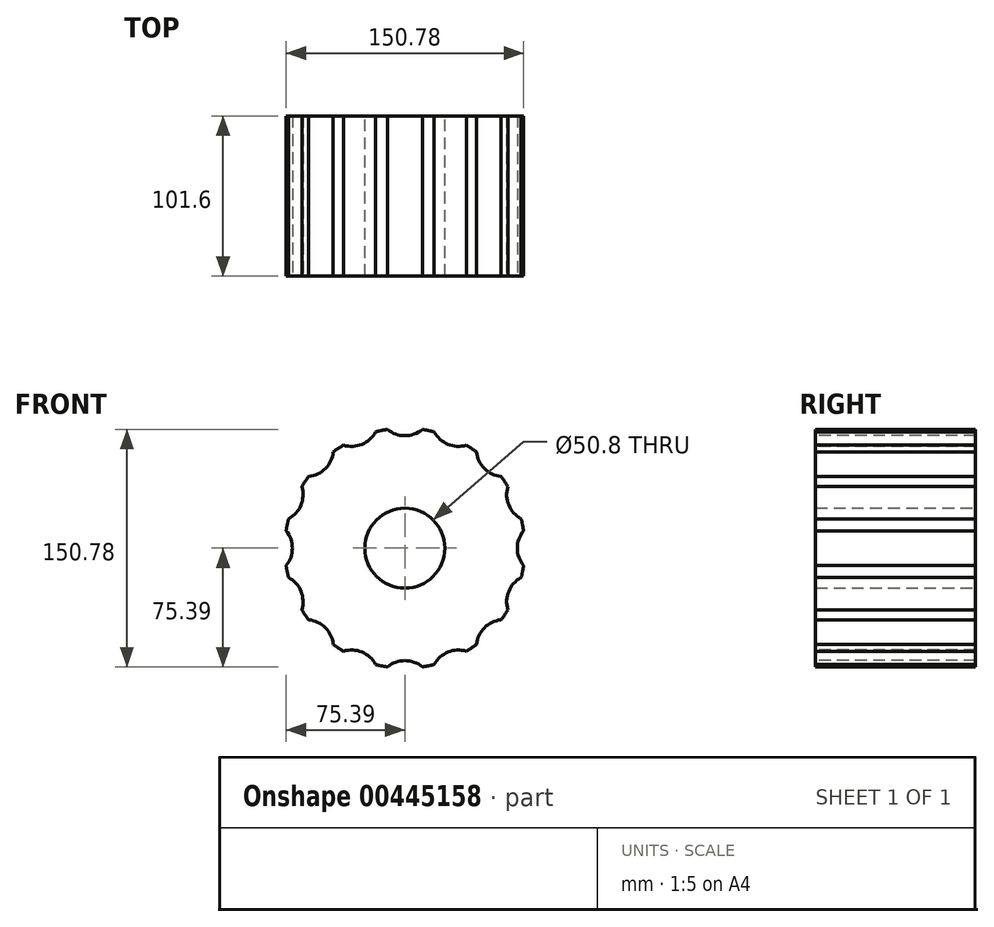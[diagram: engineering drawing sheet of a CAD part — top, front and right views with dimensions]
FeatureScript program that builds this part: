
annotation { "Feature Type Name" : "Feature", "Feature Type Description" : "" }
export const myFeature = defineFeature(function(context is Context, id is Id, definition is map)
    precondition{}
    {
        {
            var Q0;
            Q0=qCreatedBy(makeId("Front.planeOp"),FACE);
            var sketch = newSketch(context, id + "F0", { "sketchPlane" : qUnion([Q0])});
            skCircle(sketch, "E0", {"center": v(0, 0) * mm, "radius": 25.4 * mm});
            skCircle(sketch, "E1", {"center": v(0, 0) * mm, "radius": 76.2 * mm});
            skSolve(sketch);
        }
        {
            var Q0;
            Q0=makeQuery(id+"F0.imprint","IMPRINT",FACE,{"disambiguationData":[TD([[makeQuery(id+"F0.imprint","IMPRINT",EDGE,{"derivedFrom":sQuery(id+"F0.wireOp",EDGE,"E0")}),-1.0]])]});
            extrude(context, id + "F1", {"entities" : qUnion([Q0]), "depth" : 101.6 * mm});
        }
        {
            var Q0;
            Q0=makeQuery(id+"F1.opExtrude","CAP_FACE",FACE,{"disambiguationData":[OSD([sQuery(id+"F0.wireOp",EDGE,"E0"),sQuery(id+"F0.wireOp",EDGE,"E1")])],"isStart":false});
            var sketch = newSketch(context, id + "F2", { "sketchPlane" : qUnion([Q0])});
            skLineSegment(sketch, "E2", {"start": v(0, 0) * mm, "end": v(0, 76.2) * mm});
            skCircle(sketch, "E3.0", {"center": v(0, 0) * mm, "radius": 76.2 * mm});
            skLineSegment(sketch, "E4", {"start": v(0, 76.2) * mm, "end": v(0, 88.9) * mm});
            skArc(sketch, "E5", {"start": v(-11.07, 75.4) * mm, "mid": v(0, 71.44) * mm, "end": v(11.07, 75.4) * mm});
            skArc(sketch, "E6.1.0", {"start": v(-39.08, 65.42) * mm, "mid": v(-27.34, 66) * mm, "end": v(-18.63, 73.89) * mm});
            skArc(sketch, "E6.2.0", {"start": v(-61.14, 45.48) * mm, "mid": v(-50.51, 50.51) * mm, "end": v(-45.48, 61.14) * mm});
            skArc(sketch, "E6.3.0", {"start": v(-73.89, 18.63) * mm, "mid": v(-66, 27.34) * mm, "end": v(-65.42, 39.08) * mm});
            skArc(sketch, "E6.4.0", {"start": v(-75.4, -11.07) * mm, "mid": v(-71.44, 0) * mm, "end": v(-75.4, 11.07) * mm});
            skArc(sketch, "E6.5.0", {"start": v(-65.42, -39.08) * mm, "mid": v(-66, -27.34) * mm, "end": v(-73.89, -18.63) * mm});
            skArc(sketch, "E6.6.0", {"start": v(-45.48, -61.14) * mm, "mid": v(-50.51, -50.51) * mm, "end": v(-61.14, -45.48) * mm});
            skArc(sketch, "E6.7.0", {"start": v(-18.63, -73.89) * mm, "mid": v(-27.34, -66) * mm, "end": v(-39.08, -65.42) * mm});
            skArc(sketch, "E6.8.0", {"start": v(11.07, -75.4) * mm, "mid": v(0, -71.44) * mm, "end": v(-11.07, -75.4) * mm});
            skArc(sketch, "E6.9.0", {"start": v(39.08, -65.42) * mm, "mid": v(27.34, -66) * mm, "end": v(18.63, -73.89) * mm});
            skArc(sketch, "E6.10.0", {"start": v(61.14, -45.48) * mm, "mid": v(50.51, -50.51) * mm, "end": v(45.48, -61.14) * mm});
            skArc(sketch, "E6.11.0", {"start": v(73.89, -18.63) * mm, "mid": v(66, -27.34) * mm, "end": v(65.42, -39.08) * mm});
            skArc(sketch, "E6.12.0", {"start": v(75.4, 11.07) * mm, "mid": v(71.44, 0) * mm, "end": v(75.4, -11.07) * mm});
            skArc(sketch, "E6.13.0", {"start": v(65.42, 39.08) * mm, "mid": v(66, 27.34) * mm, "end": v(73.89, 18.63) * mm});
            skArc(sketch, "E6.14.0", {"start": v(45.48, 61.14) * mm, "mid": v(50.51, 50.51) * mm, "end": v(61.14, 45.48) * mm});
            skArc(sketch, "E6.15.0", {"start": v(18.63, 73.89) * mm, "mid": v(27.34, 66) * mm, "end": v(39.08, 65.42) * mm});
            skSolve(sketch);
        }
        {
            var Q0;
            {var subQ0=sQuery(id+"F2.wireOp",EDGE,"E6.15.0");Q0=makeQuery(id+"F2.imprint","IMPRINT",FACE,{"disambiguationData":[TD([[makeQuery(id+"F2.imprint","IMPRINT",EDGE,{"derivedFrom":subQ0}),1.0]])]});}
            var Q1;
            {var subQ0=sQuery(id+"F2.wireOp",EDGE,"E6.14.0");Q1=makeQuery(id+"F2.imprint","IMPRINT",FACE,{"disambiguationData":[TD([[makeQuery(id+"F2.imprint","IMPRINT",EDGE,{"derivedFrom":subQ0}),1.0]])]});}
            var Q2;
            {var subQ0=sQuery(id+"F2.wireOp",EDGE,"E6.13.0");Q2=makeQuery(id+"F2.imprint","IMPRINT",FACE,{"disambiguationData":[TD([[makeQuery(id+"F2.imprint","IMPRINT",EDGE,{"derivedFrom":subQ0}),1.0]])]});}
            var Q3;
            {var subQ0=sQuery(id+"F2.wireOp",EDGE,"E6.12.0");Q3=makeQuery(id+"F2.imprint","IMPRINT",FACE,{"disambiguationData":[TD([[makeQuery(id+"F2.imprint","IMPRINT",EDGE,{"derivedFrom":subQ0}),1.0]])]});}
            var Q4;
            {var subQ0=sQuery(id+"F2.wireOp",EDGE,"E6.11.0");Q4=makeQuery(id+"F2.imprint","IMPRINT",FACE,{"disambiguationData":[TD([[makeQuery(id+"F2.imprint","IMPRINT",EDGE,{"derivedFrom":subQ0}),1.0]])]});}
            var Q5;
            {var subQ0=sQuery(id+"F2.wireOp",EDGE,"E6.10.0");Q5=makeQuery(id+"F2.imprint","IMPRINT",FACE,{"disambiguationData":[TD([[makeQuery(id+"F2.imprint","IMPRINT",EDGE,{"derivedFrom":subQ0}),1.0]])]});}
            var Q6;
            {var subQ0=sQuery(id+"F2.wireOp",EDGE,"E6.9.0");Q6=makeQuery(id+"F2.imprint","IMPRINT",FACE,{"disambiguationData":[TD([[makeQuery(id+"F2.imprint","IMPRINT",EDGE,{"derivedFrom":subQ0}),1.0]])]});}
            var Q7;
            {var subQ0=sQuery(id+"F2.wireOp",EDGE,"E6.8.0");Q7=makeQuery(id+"F2.imprint","IMPRINT",FACE,{"disambiguationData":[TD([[makeQuery(id+"F2.imprint","IMPRINT",EDGE,{"derivedFrom":subQ0}),1.0]])]});}
            var Q8;
            {var subQ0=sQuery(id+"F2.wireOp",EDGE,"E6.7.0");Q8=makeQuery(id+"F2.imprint","IMPRINT",FACE,{"disambiguationData":[TD([[makeQuery(id+"F2.imprint","IMPRINT",EDGE,{"derivedFrom":subQ0}),1.0]])]});}
            var Q9;
            {var subQ0=sQuery(id+"F2.wireOp",EDGE,"E6.6.0");Q9=makeQuery(id+"F2.imprint","IMPRINT",FACE,{"disambiguationData":[TD([[makeQuery(id+"F2.imprint","IMPRINT",EDGE,{"derivedFrom":subQ0}),1.0]])]});}
            var Q10;
            {var subQ0=sQuery(id+"F2.wireOp",EDGE,"E6.5.0");Q10=makeQuery(id+"F2.imprint","IMPRINT",FACE,{"disambiguationData":[TD([[makeQuery(id+"F2.imprint","IMPRINT",EDGE,{"derivedFrom":subQ0}),1.0]])]});}
            var Q11;
            {var subQ0=sQuery(id+"F2.wireOp",EDGE,"E6.4.0");Q11=makeQuery(id+"F2.imprint","IMPRINT",FACE,{"disambiguationData":[TD([[makeQuery(id+"F2.imprint","IMPRINT",EDGE,{"derivedFrom":subQ0}),1.0]])]});}
            var Q12;
            {var subQ0=sQuery(id+"F2.wireOp",EDGE,"E6.3.0");Q12=makeQuery(id+"F2.imprint","IMPRINT",FACE,{"disambiguationData":[TD([[makeQuery(id+"F2.imprint","IMPRINT",EDGE,{"derivedFrom":subQ0}),1.0]])]});}
            var Q13;
            {var subQ0=sQuery(id+"F2.wireOp",EDGE,"E6.2.0");Q13=makeQuery(id+"F2.imprint","IMPRINT",FACE,{"disambiguationData":[TD([[makeQuery(id+"F2.imprint","IMPRINT",EDGE,{"derivedFrom":subQ0}),1.0]])]});}
            var Q14;
            {var subQ0=sQuery(id+"F2.wireOp",EDGE,"E6.1.0");Q14=makeQuery(id+"F2.imprint","IMPRINT",FACE,{"disambiguationData":[TD([[makeQuery(id+"F2.imprint","IMPRINT",EDGE,{"derivedFrom":subQ0}),1.0]])]});}
            var Q15;
            {var subQ0=sQuery(id+"F2.wireOp",EDGE,"E3.0");var subQ1=sQuery(id+"F2.wireOp",EDGE,"E2");var subQ2=makeQuery(id+"F2.imprint","INTERSECT",VERTEX,{"derivedFrom":[subQ1,subQ0]});Q15=makeQuery(id+"F2.imprint","IMPRINT",FACE,{"disambiguationData":[TD([[makeQuery(id+"F2.imprint","IMPRINT",EDGE,{"disambiguationData":[TD([[subQ2,1.0]])],"derivedFrom":subQ1}),-1.0]])]});}
            var Q16;
            {var subQ0=sQuery(id+"F2.wireOp",EDGE,"E3.0");var subQ1=sQuery(id+"F2.wireOp",EDGE,"E2");var subQ2=makeQuery(id+"F2.imprint","INTERSECT",VERTEX,{"derivedFrom":[subQ1,subQ0]});Q16=makeQuery(id+"F2.imprint","IMPRINT",FACE,{"disambiguationData":[TD([[makeQuery(id+"F2.imprint","IMPRINT",EDGE,{"disambiguationData":[TD([[subQ2,1.0]])],"derivedFrom":subQ1}),1.0]])]});}
            extrude(context, id + "F3", {"entities" : qUnion([Q0, Q1, Q2, Q3, Q4, Q5, Q6, Q7, Q8, Q9, Q10, Q11, Q12, Q13, Q14, Q15, Q16]), "operationType" : NewBodyOperationType.REMOVE, "oppositeDirection" : true, "depth" : 101.6 * mm});
        }
    });
